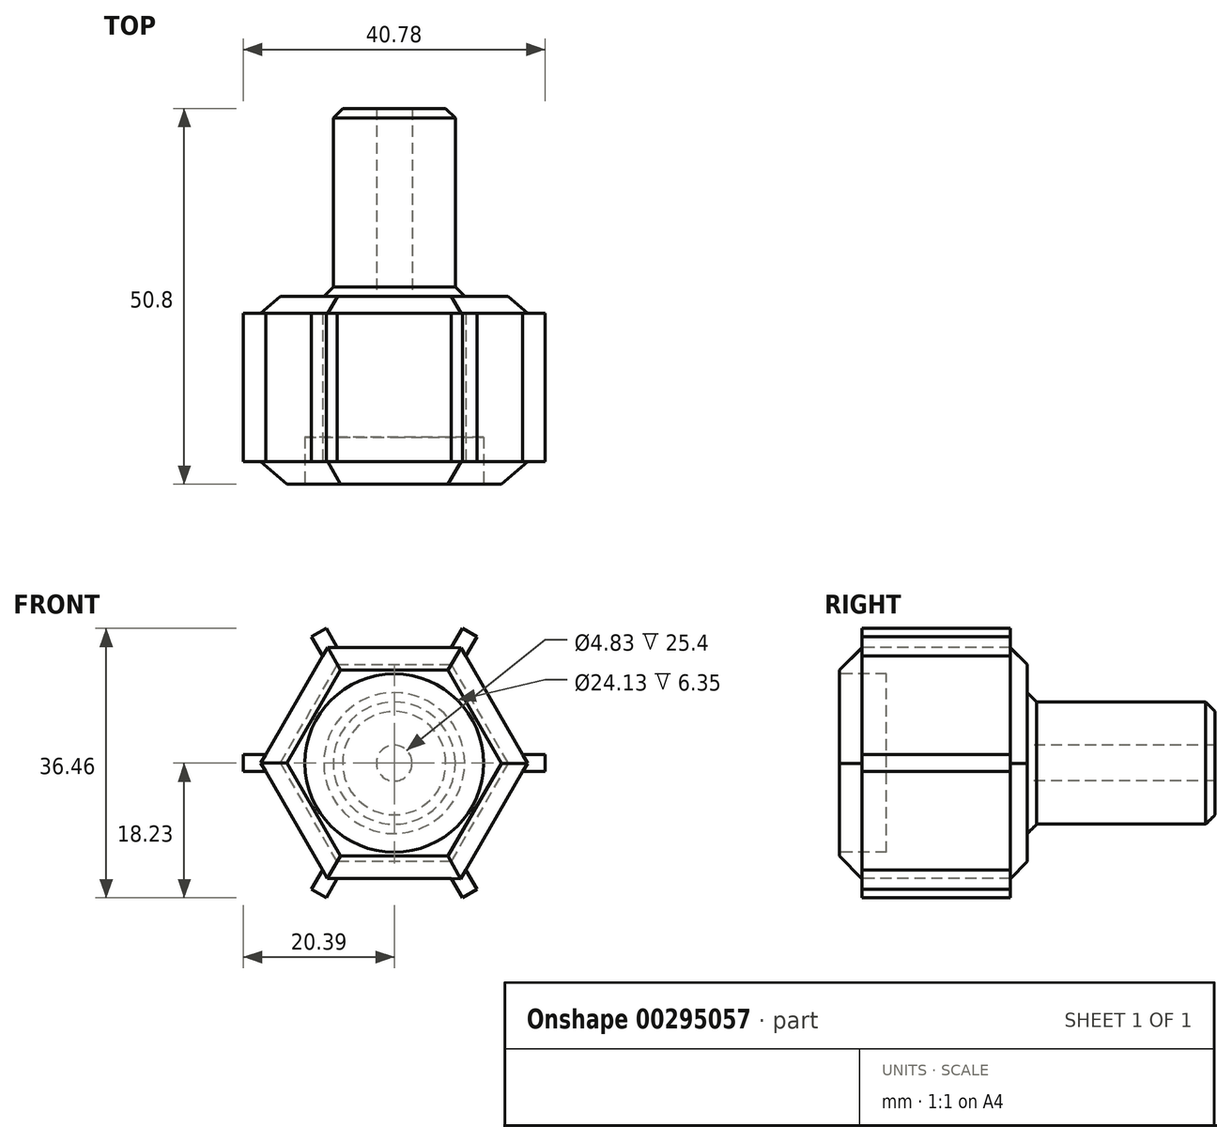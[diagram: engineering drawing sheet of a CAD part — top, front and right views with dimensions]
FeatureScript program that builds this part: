
annotation { "Feature Type Name" : "Feature", "Feature Type Description" : "" }
export const myFeature = defineFeature(function(context is Context, id is Id, definition is map)
    precondition{}
    {
        {
            var Q0;
            Q0=qCreatedBy(makeId("Front.planeOp"),FACE);
            var sketch = newSketch(context, id + "F0", { "sketchPlane" : qUnion([Q0])});
            skCircle(sketch, "E0.cCircle", {"center": v(0, 0) * mm, "radius": 15.62 * mm, "construction": true});
            skLineSegment(sketch, "E0.0", {"start": v(9.04, 15.6) * mm, "end": v(18.04, -0.03) * mm});
            skLineSegment(sketch, "E0.1", {"start": v(18.04, -0.03) * mm, "end": v(9, -15.64) * mm});
            skLineSegment(sketch, "E0.2", {"start": v(9, -15.64) * mm, "end": v(-9.04, -15.6) * mm});
            skLineSegment(sketch, "E0.3", {"start": v(-9.04, -15.6) * mm, "end": v(-18.04, 0.03) * mm});
            skLineSegment(sketch, "E0.4", {"start": v(-18.04, 0.03) * mm, "end": v(-9, 15.64) * mm});
            skLineSegment(sketch, "E0.5", {"start": v(-9, 15.64) * mm, "end": v(9.04, 15.6) * mm});
            skPoint(sketch, "E0.0.midPoint", {"position": v(13.54, 7.79) * mm});
            skSolve(sketch);
        }
        {
            var Q0;
            Q0=makeQuery(id+"F0.imprint","IMPRINT",FACE,{"disambiguationData":[TD([[makeQuery(id+"F0.imprint","IMPRINT",EDGE,{"derivedFrom":sQuery(id+"F0.wireOp",EDGE,"E0.0")}),-1.0]])]});
            extrude(context, id + "F1", {"entities" : qUnion([Q0]), "depth" : 25.4 * mm});
        }
        {
            var Q0;
            Q0=qCreatedBy(makeId("Front.planeOp"),FACE);
            cPlane(context, id + "F2", {"entities" : qUnion([Q0]), "cplaneType" : CPlaneType.OFFSET, "offset" : 2.3 * mm, "width" : 152.4 * mm, "height" : 152.4 * mm});
        }
        {
            var Q0;
            Q0=qCreatedBy(id+"F2.planeOp",FACE);
            var sketch = newSketch(context, id + "F3", { "sketchPlane" : qUnion([Q0])});
            skLineSegment(sketch, "E1.bottom", {"start": v(17.35, 1.14) * mm, "end": v(20.4, 1.14) * mm});
            skLineSegment(sketch, "E1.top", {"start": v(17.35, -1.14) * mm, "end": v(20.4, -1.14) * mm});
            skLineSegment(sketch, "E1.left", {"start": v(17.35, 1.14) * mm, "end": v(17.35, -1.14) * mm});
            skLineSegment(sketch, "E1.right", {"start": v(20.4, 1.14) * mm, "end": v(20.4, -1.14) * mm});
            skLineSegment(sketch, "E2.1.0", {"start": v(7.68, 15.6) * mm, "end": v(9.2, 18.23) * mm});
            skLineSegment(sketch, "E2.1.1", {"start": v(7.68, 15.6) * mm, "end": v(9.66, 14.45) * mm});
            skLineSegment(sketch, "E2.1.2", {"start": v(9.66, 14.45) * mm, "end": v(11.19, 17.1) * mm});
            skLineSegment(sketch, "E2.1.3", {"start": v(9.2, 18.23) * mm, "end": v(11.19, 17.1) * mm});
            skLineSegment(sketch, "E2.2.0", {"start": v(-9.66, 14.45) * mm, "end": v(-11.19, 17.1) * mm});
            skLineSegment(sketch, "E2.2.1", {"start": v(-9.66, 14.45) * mm, "end": v(-7.68, 15.6) * mm});
            skLineSegment(sketch, "E2.2.2", {"start": v(-7.68, 15.6) * mm, "end": v(-9.2, 18.23) * mm});
            skLineSegment(sketch, "E2.2.3", {"start": v(-11.19, 17.1) * mm, "end": v(-9.2, 18.23) * mm});
            skLineSegment(sketch, "E2.3.0", {"start": v(-17.35, -1.14) * mm, "end": v(-20.4, -1.14) * mm});
            skLineSegment(sketch, "E2.3.1", {"start": v(-17.35, -1.14) * mm, "end": v(-17.35, 1.14) * mm});
            skLineSegment(sketch, "E2.3.2", {"start": v(-17.35, 1.14) * mm, "end": v(-20.4, 1.14) * mm});
            skLineSegment(sketch, "E2.3.3", {"start": v(-20.4, -1.14) * mm, "end": v(-20.4, 1.14) * mm});
            skLineSegment(sketch, "E2.4.0", {"start": v(-7.68, -15.6) * mm, "end": v(-9.2, -18.23) * mm});
            skLineSegment(sketch, "E2.4.1", {"start": v(-7.68, -15.6) * mm, "end": v(-9.66, -14.45) * mm});
            skLineSegment(sketch, "E2.4.2", {"start": v(-9.66, -14.45) * mm, "end": v(-11.19, -17.1) * mm});
            skLineSegment(sketch, "E2.4.3", {"start": v(-9.2, -18.23) * mm, "end": v(-11.19, -17.1) * mm});
            skLineSegment(sketch, "E2.5.0", {"start": v(9.66, -14.45) * mm, "end": v(11.19, -17.1) * mm});
            skLineSegment(sketch, "E2.5.1", {"start": v(9.66, -14.45) * mm, "end": v(7.68, -15.6) * mm});
            skLineSegment(sketch, "E2.5.2", {"start": v(7.68, -15.6) * mm, "end": v(9.2, -18.23) * mm});
            skLineSegment(sketch, "E2.5.3", {"start": v(11.19, -17.1) * mm, "end": v(9.2, -18.23) * mm});
            skPoint(sketch, "E2.center", {"position": v(0, 0) * mm});
            skSolve(sketch);
        }
        {
            var Q0;
            Q0=makeQuery(id+"F1.opExtrude","CAP_FACE",FACE,{"disambiguationData":[OSD([sQuery(id+"F0.wireOp",EDGE,"E0.0"),sQuery(id+"F0.wireOp",EDGE,"E0.1"),sQuery(id+"F0.wireOp",EDGE,"E0.2"),sQuery(id+"F0.wireOp",EDGE,"E0.3"),sQuery(id+"F0.wireOp",EDGE,"E0.4"),sQuery(id+"F0.wireOp",EDGE,"E0.5")])],"isStart":true});
            chamfer(context, id + "F4", {"entities" : qUnion([Q0]), "width" : 2.3 * mm, "tangentPropagation" : true});
        }
        {
            var Q0;
            Q0=makeQuery(id+"F1.opExtrude","CAP_FACE",FACE,{"disambiguationData":[OSD([sQuery(id+"F0.wireOp",EDGE,"E0.0"),sQuery(id+"F0.wireOp",EDGE,"E0.1"),sQuery(id+"F0.wireOp",EDGE,"E0.2"),sQuery(id+"F0.wireOp",EDGE,"E0.3"),sQuery(id+"F0.wireOp",EDGE,"E0.4"),sQuery(id+"F0.wireOp",EDGE,"E0.5")])],"isStart":false});
            chamfer(context, id + "F5", {"entities" : qUnion([Q0]), "width" : 3.05 * mm, "tangentPropagation" : true});
        }
        {
            var Q0;
            Q0 = qSketchRegion(id + "F3", true);
            extrude(context, id + "F6", {"entities" : qUnion([Q0]), "operationType" : NewBodyOperationType.ADD, "depth" : 20.07 * mm});
        }
        {
            var Q0;
            Q0=qCreatedBy(makeId("Front.planeOp"),FACE);
            var sketch = newSketch(context, id + "F7", { "sketchPlane" : qUnion([Q0])});
            skCircle(sketch, "E3", {"center": v(0, 0) * mm, "radius": 8.26 * mm});
            skSolve(sketch);
        }
        {
            var Q0;
            Q0=qCreatedBy(makeId("Front.planeOp"),FACE);
            var sketch = newSketch(context, id + "F8", { "sketchPlane" : qUnion([Q0])});
            skCircle(sketch, "E4", {"center": v(0, 0) * mm, "radius": 2.41 * mm});
            skSolve(sketch);
        }
        {
            var Q0;
            Q0=makeQuery(id+"F7.imprint","IMPRINT",FACE,{"disambiguationData":[TD([[makeQuery(id+"F7.imprint","IMPRINT",EDGE,{"derivedFrom":sQuery(id+"F7.wireOp",EDGE,"E3")}),1.0]])]});
            extrude(context, id + "F9", {"entities" : qUnion([Q0]), "operationType" : NewBodyOperationType.ADD, "oppositeDirection" : true, "depth" : 25.4 * mm});
        }
        {
            var Q0;
            Q0 = qSketchRegion(id + "F8", true);
            extrude(context, id + "F10", {"entities" : qUnion([Q0]), "operationType" : NewBodyOperationType.REMOVE, "oppositeDirection" : true, "depth" : 25.4 * mm});
        }
        {
            var Q0;
            Q0=makeQuery(id+"F9.opExtrude","SWEPT_FACE",FACE,{"disambiguationData":[OSD([sQuery(id+"F7.wireOp",EDGE,"E3")])]});
            chamfer(context, id + "F11", {"entities" : qUnion([Q0]), "width" : 1.27 * mm, "tangentPropagation" : true});
        }
        {
            var Q0;
            Q0=qCreatedBy(makeId("Front.planeOp"),FACE);
            cPlane(context, id + "F12", {"entities" : qUnion([Q0]), "cplaneType" : CPlaneType.OFFSET, "offset" : 25.4 * mm, "width" : 152.4 * mm, "height" : 152.4 * mm});
        }
        {
            var Q0;
            Q0=qCreatedBy(id+"F12.planeOp",FACE);
            var sketch = newSketch(context, id + "F13", { "sketchPlane" : qUnion([Q0])});
            skCircle(sketch, "E5", {"center": v(0, 0) * mm, "radius": 12.07 * mm});
            skSolve(sketch);
        }
        {
            var Q0;
            Q0=makeQuery(id+"F13.imprint","IMPRINT",FACE,{"disambiguationData":[TD([[makeQuery(id+"F13.imprint","IMPRINT",EDGE,{"derivedFrom":sQuery(id+"F13.wireOp",EDGE,"E5")}),1.0]])]});
            extrude(context, id + "F14", {"entities" : qUnion([Q0]), "operationType" : NewBodyOperationType.REMOVE, "oppositeDirection" : true, "depth" : 6.35 * mm});
        }
    });
